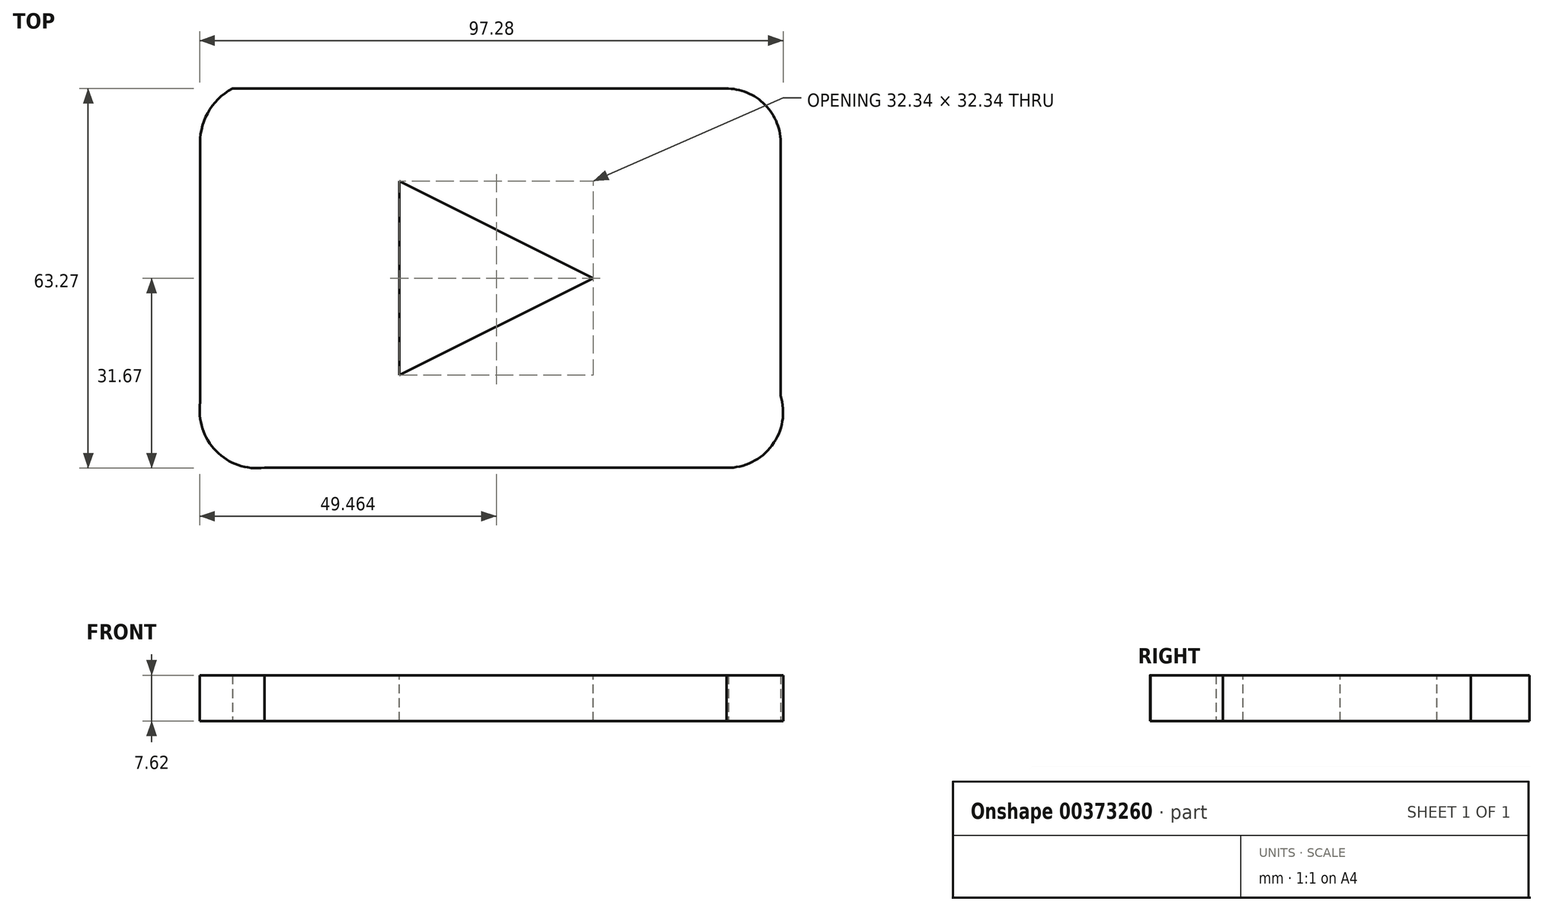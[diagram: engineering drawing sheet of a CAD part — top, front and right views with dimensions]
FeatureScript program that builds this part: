
annotation { "Feature Type Name" : "Feature", "Feature Type Description" : "" }
export const myFeature = defineFeature(function(context is Context, id is Id, definition is map)
    precondition{}
    {
        {
            var Q0;
            Q0=qCreatedBy(makeId("Top.planeOp"),FACE);
            var sketch = newSketch(context, id + "F0", { "sketchPlane" : qUnion([Q0])});
            skLineSegment(sketch, "E0.bottom", {"start": v(39.65, 31.6) * mm, "end": v(-43.03, 31.6) * mm});
            skLineSegment(sketch, "E0.top", {"start": v(39.66, -31.6) * mm, "end": v(-40.11, -31.6) * mm});
            skLineSegment(sketch, "E0.left", {"start": v(48.37, 23.22) * mm, "end": v(48.37, -25.09) * mm});
            skLineSegment(sketch, "E0.right", {"start": v(-48.37, 23.38) * mm, "end": v(-48.37, -23.52) * mm});
            skPoint(sketch, "E0.middle", {"position": v(0, 0) * mm});
            skArc(sketch, "E1", {"start": v(-43.03, 31.6) * mm, "mid": v(-47.15, 27.49) * mm, "end": v(-48.37, 21.8) * mm});
            skPoint(sketch, "E2.orphan", {"position": v(-48.37, 31.6) * mm});
            skArc(sketch, "E3", {"start": v(48.37, 21.8) * mm, "mid": v(46.1, 28.55) * mm, "end": v(39.65, 31.6) * mm});
            skPoint(sketch, "E4.orphan", {"position": v(48.37, 31.6) * mm});
            skArc(sketch, "E5", {"start": v(-48.37, -20.67) * mm, "mid": v(-45.75, -28.8) * mm, "end": v(-37.68, -31.6) * mm});
            skPoint(sketch, "E6.orphan", {"position": v(-48.37, -31.6) * mm});
            skArc(sketch, "E7", {"start": v(39.37, -31.6) * mm, "mid": v(46.95, -27.87) * mm, "end": v(48.37, -19.55) * mm});
            skPoint(sketch, "E8.orphan", {"position": v(48.37, -31.6) * mm});
            skSolve(sketch);
        }
        {
            var Q0;
            Q0 = qSketchRegion(id + "F0", true);
            extrude(context, id + "F1", {"entities" : qUnion([Q0]), "depth" : 7.62 * mm});
        }
        {
            var Q0;
            Q0=makeQuery(id+"F1.opExtrude","CAP_FACE",FACE,{"disambiguationData":[OSD([sQuery(id+"F0.wireOp",EDGE,"E0.bottom"),sQuery(id+"F0.wireOp",EDGE,"E0.top"),sQuery(id+"F0.wireOp",EDGE,"E0.left"),sQuery(id+"F0.wireOp",EDGE,"E0.right"),sQuery(id+"F0.wireOp",EDGE,"E1"),sQuery(id+"F0.wireOp",EDGE,"E3"),sQuery(id+"F0.wireOp",EDGE,"E5"),sQuery(id+"F0.wireOp",EDGE,"E7")])],"isStart":false});
            var sketch = newSketch(context, id + "F2", { "sketchPlane" : qUnion([Q0])});
            skLineSegment(sketch, "E9", {"start": v(-15.19, 16.17) * mm, "end": v(-15.19, -16.17) * mm});
            skLineSegment(sketch, "E10", {"start": v(-15.19, -16.17) * mm, "end": v(17.16, 0) * mm});
            skLineSegment(sketch, "E11", {"start": v(-15.19, 16.17) * mm, "end": v(17.16, 0) * mm});
            skSolve(sketch);
        }
        {
            var Q0;
            Q0 = qSketchRegion(id + "F2", true);
            extrude(context, id + "F3", {"entities" : qUnion([Q0]), "operationType" : NewBodyOperationType.REMOVE, "oppositeDirection" : true, "depth" : 7.62 * mm});
        }
    });
